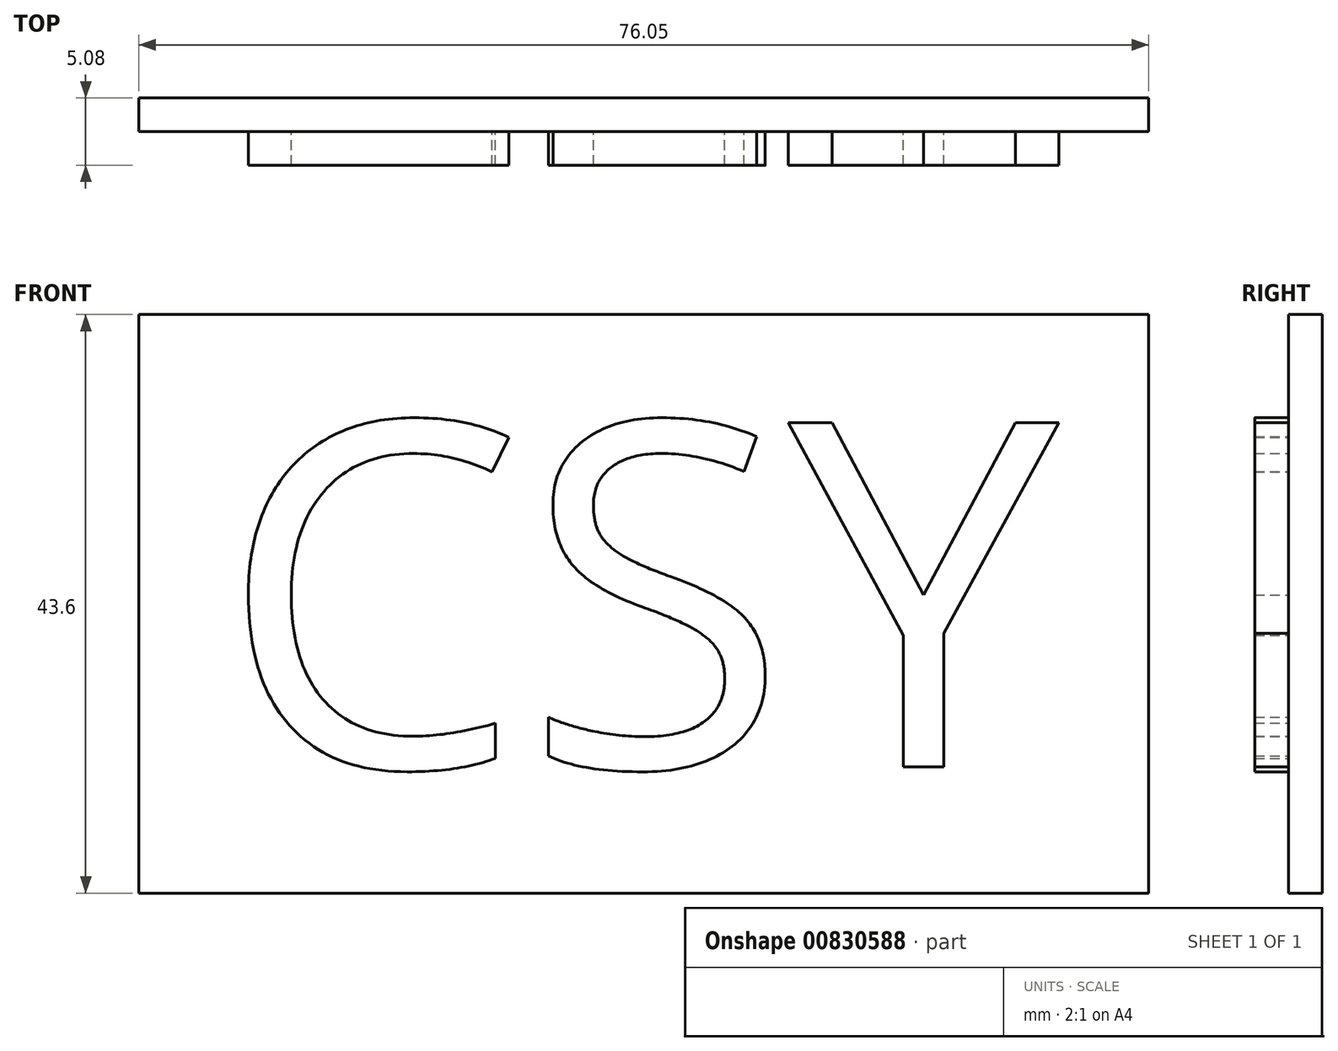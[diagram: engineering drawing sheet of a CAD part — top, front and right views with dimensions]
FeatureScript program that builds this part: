
annotation { "Feature Type Name" : "Feature", "Feature Type Description" : "" }
export const myFeature = defineFeature(function(context is Context, id is Id, definition is map)
    precondition{}
    {
        {
            var Q0;
            Q0=qCreatedBy(makeId("Front.planeOp"),FACE);
            var sketch = newSketch(context, id + "F0", { "sketchPlane" : qUnion([Q0])});
            skLineSegment(sketch, "E0.bottom", {"start": v(0, 0) * mm, "end": v(76.05, 0) * mm});
            skLineSegment(sketch, "E0.top", {"start": v(0, 43.6) * mm, "end": v(76.05, 43.6) * mm});
            skLineSegment(sketch, "E0.left", {"start": v(0, 0) * mm, "end": v(0, 43.6) * mm});
            skLineSegment(sketch, "E0.right", {"start": v(76.05, 0) * mm, "end": v(76.05, 43.6) * mm});
            skSolve(sketch);
        }
        {
            var Q0;
            Q0=makeQuery(id+"F0.imprint","IMPRINT",FACE,{"disambiguationData":[TD([[makeQuery(id+"F0.imprint","IMPRINT",EDGE,{"derivedFrom":sQuery(id+"F0.wireOp",EDGE,"E0.bottom")}),1.0]])]});
            extrude(context, id + "F1", {"entities" : qUnion([Q0]), "depth" : 2.54 * mm, "offsetDistance" : 25.4 * mm});
        }
        {
            var Q0;
            Q0=makeQuery(id+"F1.opExtrude","CAP_FACE",FACE,{"disambiguationData":[OSD([sQuery(id+"F0.wireOp",EDGE,"E0.bottom"),sQuery(id+"F0.wireOp",EDGE,"E0.top"),sQuery(id+"F0.wireOp",EDGE,"E0.left"),sQuery(id+"F0.wireOp",EDGE,"E0.right")])],"isStart":false});
            var sketch = newSketch(context, id + "F2", { "sketchPlane" : qUnion([Q0])});
            skText(sketch, "E1", { "text": "CSY", "fontName": "OpenSans-Regular.ttf"});
            const initialGuessF2  = {"E1": [0.00602, 0.0095, 1, 0, 0.02618]};
            skSetInitialGuess(sketch, initialGuessF2);
            skSolve(sketch);
        }
        {
            var Q0;
            Q0 = qSketchRegion(id + "F2", true);
            extrude(context, id + "F3", {"entities" : qUnion([Q0]), "operationType" : NewBodyOperationType.ADD, "depth" : 2.54 * mm, "offsetDistance" : 25.4 * mm});
        }
    });
